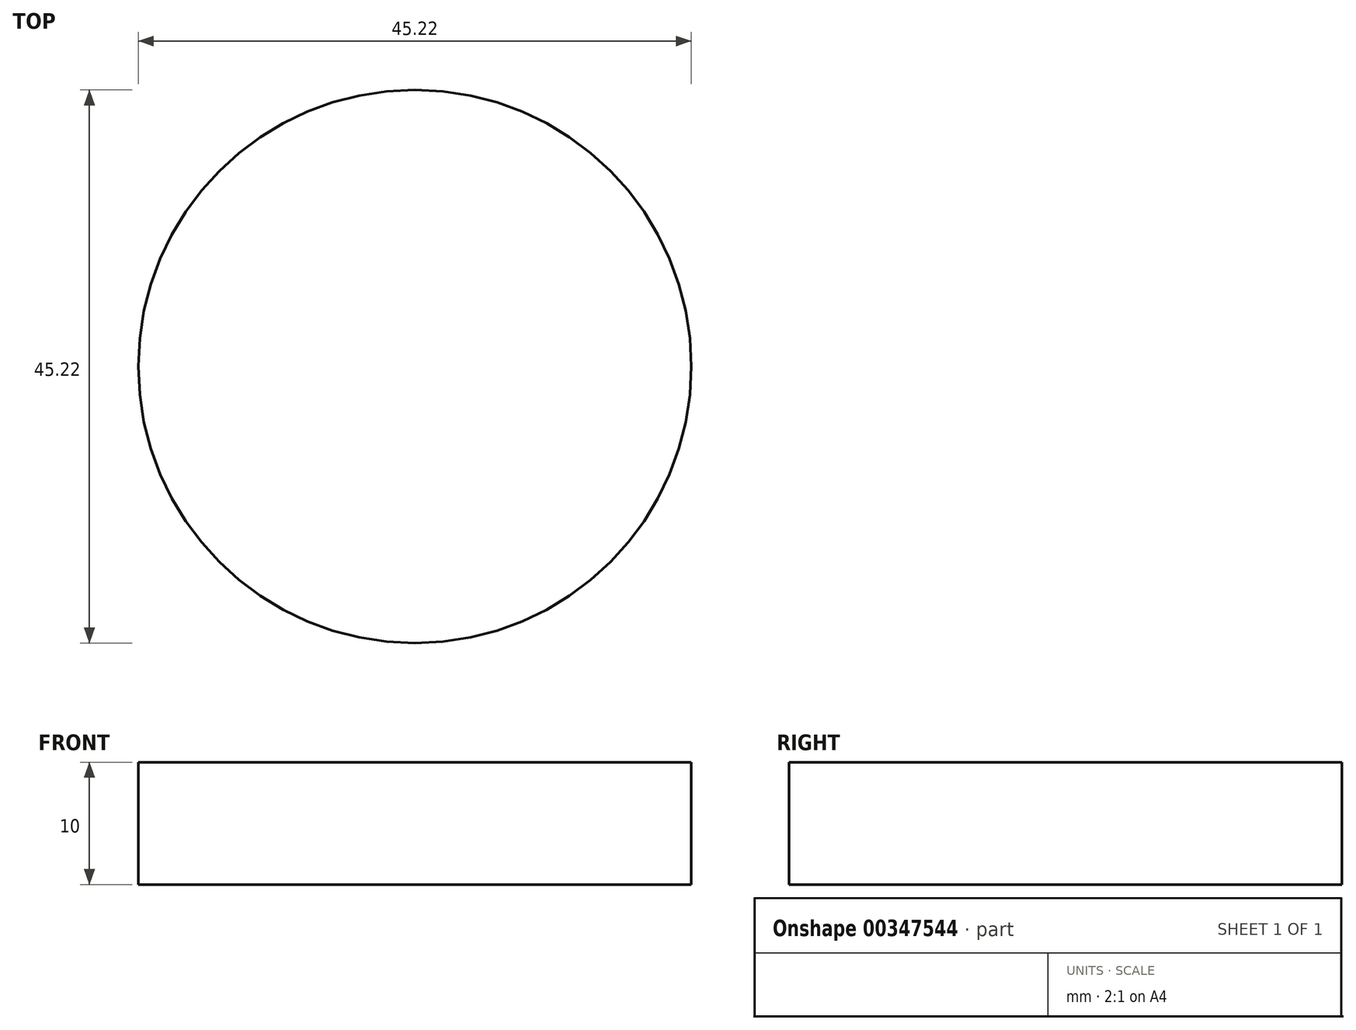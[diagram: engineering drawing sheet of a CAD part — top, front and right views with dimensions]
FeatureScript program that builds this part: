
annotation { "Feature Type Name" : "Feature", "Feature Type Description" : "" }
export const myFeature = defineFeature(function(context is Context, id is Id, definition is map)
    precondition{}
    {
        {
            var Q0;
            Q0=qCreatedBy(makeId("Top.planeOp"),FACE);
            var sketch = newSketch(context, id + "F0", { "sketchPlane" : qUnion([Q0])});
            skCircle(sketch, "E0", {"center": v(0, 0) * mm, "radius": 22.61 * mm});
            skSolve(sketch);
        }
        {
            var Q0;
            Q0=makeQuery(id+"F0.imprint","IMPRINT",FACE,{"disambiguationData":[TD([[makeQuery(id+"F0.imprint","IMPRINT",EDGE,{"derivedFrom":sQuery(id+"F0.wireOp",EDGE,"E0")}),1.0]])]});
            extrude(context, id + "F1", {"entities" : qUnion([Q0]), "depth" : 10 * mm});
        }
    });
